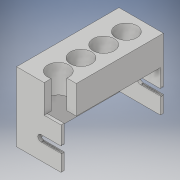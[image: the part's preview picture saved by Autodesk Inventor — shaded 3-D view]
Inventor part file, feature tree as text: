
AUTODESK INVENTOR PART (.ipt)
format: ipt  version: 2018 (Build 220112000, 112)  size: 282,624 bytes
history: native  units: in
note: dims shown in document units (in); Inventor stores cm internally (conversion verified against a paired STEP export)
features: extrude x13, sketch x12, projected_geometry x8, plane x1, mirror x1
ambient origin geometry x8: Origin, YZ Plane, XZ Plane, XY Plane, X Axis, Y Axis, Z Axis, Center Point
bodies: Solid1 (feature_tree)
feature tree (35):
  extrude  "Extrusion1"  Depth=9.0in
  extrude  "Extrusion2"  Depth=15.7in
  extrude  "Extrusion3"  Depth=0.5in
  extrude  "Extrusion4"  Depth=0.5in TaperAngle=0.0deg
  extrude  "Extrusion5"  Depth=1.05in
  extrude  "Extrusion6"  Depth=18.0in TaperAngle=0.0deg
  extrude  "Extrusion7"  Depth=3.25in
  extrude  "Extrusion11"  Depth=3.45in
  extrude  "Extrusion12"  Depth=3.25in
  plane  "Work Plane1"
  mirror  "Mirror1"
  extrude  "Extrusion18"  Depth=2.1in TaperAngle=0.0deg
  extrude  "Extrusion8"  Depth=0.75in TaperAngle=0.0deg
  extrude  "Extrusion9"  Depth=4.6in
  extrude  "Extrusion10"  Depth=4.6in
  sketch  "Sketch1"  dims[d0=16.7in d1=9.0in]
  sketch  "Sketch2"  dims[d2=6.5in d3=0.0in d4=15.7in]
  sketch  "Sketch4"  dims[d5=6.5in d6=0.5in]
  projected_geometry  "Projected Loop1"
  sketch  "Sketch5"  dims[d7=0.5in d8=5.85in d9=0.0in]
  projected_geometry  "Projected Loop2"
  sketch  "Sketch7"  dims[d10=3.775in d11=1.05in]
  projected_geometry  "Projected Loop4"
  sketch  "Sketch8"  dims[d12=2.475in d13=18.0in d14=0.0in]
  projected_geometry  "Projected Loop5"
  sketch  "Sketch9"  dims[d15=3.45in d16=3.25in]
  projected_geometry  "Projected Loop6"
  sketch  "Sketch10"  dims[d17=2.3in d18=3.45in]
  projected_geometry  "Projected Loop7"
  sketch  "Sketch11"  dims[d19=3.7in d20=3.25in]
  sketch  "Sketch12"  dims[d21=3.0in d22=0.0in d23=2.1in d24=0.0in]
  projected_geometry  "Projected Loop8"
  sketch  "Sketch13"  dims[d25=0.75in d26=0.0in d27=0.75in d28=0.0in]
  projected_geometry  "Projected Loop9"
  sketch  "Sketch21"  dims[d29=0.75in d30=0.75in d31=0.75in d32=0.75in d33=4.95in d34=4.95in d35=4.95in d36=4.95in d37=4.0in d38=0.0in d39=0.0in d40=1.5in d41=0.0in d42=1.5in d43=0.0in d44=0.24in d45=0.12in d46=0.13in d47=3.25in d48=0.0in d49=0.2in d50=0.0in d70=2.5in d71=2.75in d72=4.6in d73=0.0in]
